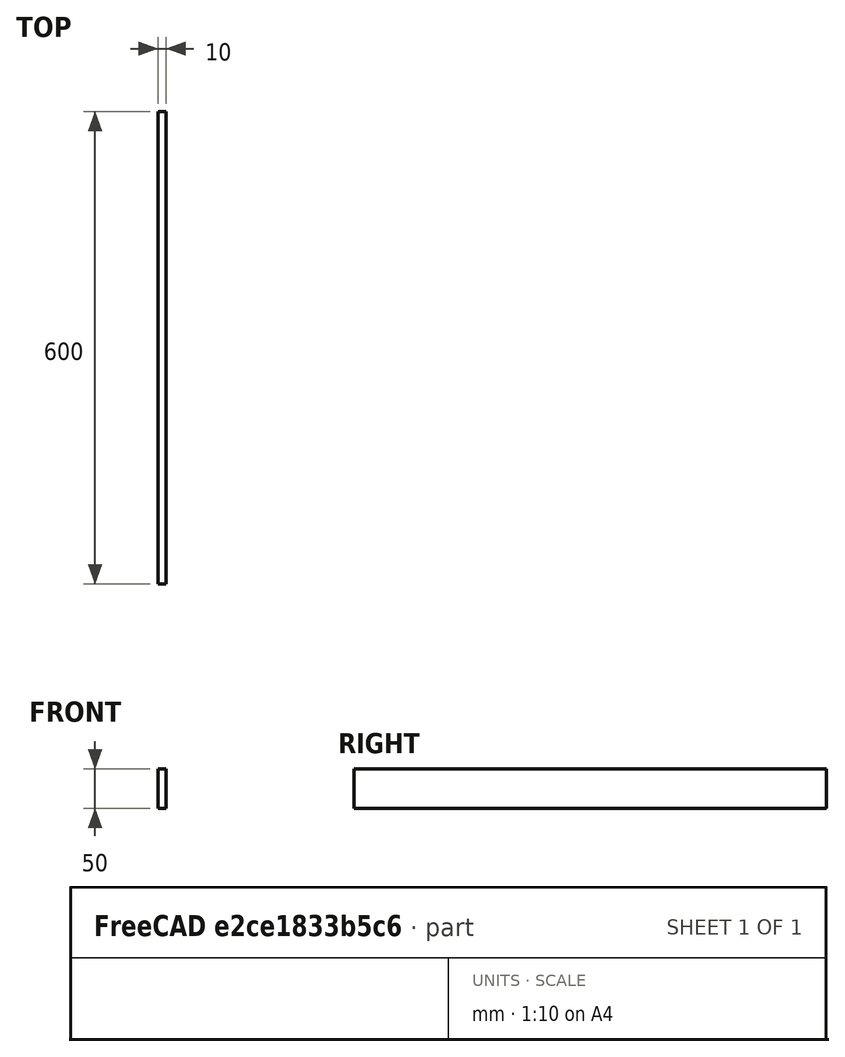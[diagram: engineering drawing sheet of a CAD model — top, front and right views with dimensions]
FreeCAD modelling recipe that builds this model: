
FCSTD DOCUMENT  (FreeCAD 0.14R3702 (Git))
Label: Base_CaraLarga
License: All rights reserved
LicenseURL: http://en.wikipedia.org/wiki/All_rights_reserved
objects: Sketcher::SketchObject×1, PartDesign::Pad×1
note: 3 computed .brp shape members not serialized (recipe doc carries the construction recipe); baked Part::Feature solids carry a one-line shape summary decoded from their .brp

FEATURE [Sketcher::SketchObject] Sketch
  Placement = pos=(0,300,0) rot=(1,0,0;1.5708rad)
  sketch-geometry (4):
    g0: LineSegment StartX=-300 StartY=25 StartZ=0 EndX=300 EndY=25 EndZ=0
    g1: LineSegment StartX=300 StartY=25 StartZ=0 EndX=300 EndY=-25 EndZ=0
    g2: LineSegment StartX=300 StartY=-25 StartZ=0 EndX=-300 EndY=-25 EndZ=0
    g3: LineSegment StartX=-300 StartY=-25 StartZ=0 EndX=-300 EndY=25 EndZ=0
  constraints (12):
    c: Coincident(g0,g1)
    c: Coincident(g1,g2)
    c: Coincident(g2,g3)
    c: Coincident(g3,g0)
    c: Horizontal(g0)
    c: Horizontal(g2)
    c: Vertical(g1)
    c: Vertical(g3)
    c: DistanceY(g1) = -50
    c: DistanceX(g0) = 600
    c: DistanceX(g-1,g0) = -300
    c: DistanceY(g-1,g2) = -25
FEATURE [PartDesign::Pad] Pad
  Length = 10
  Length2 = 100
  Placement = pos=(0,0,0) rot=(0.57735,0.57735,0.57735;2.0944rad)
  Sketch = -> Sketch
  Type = 0
